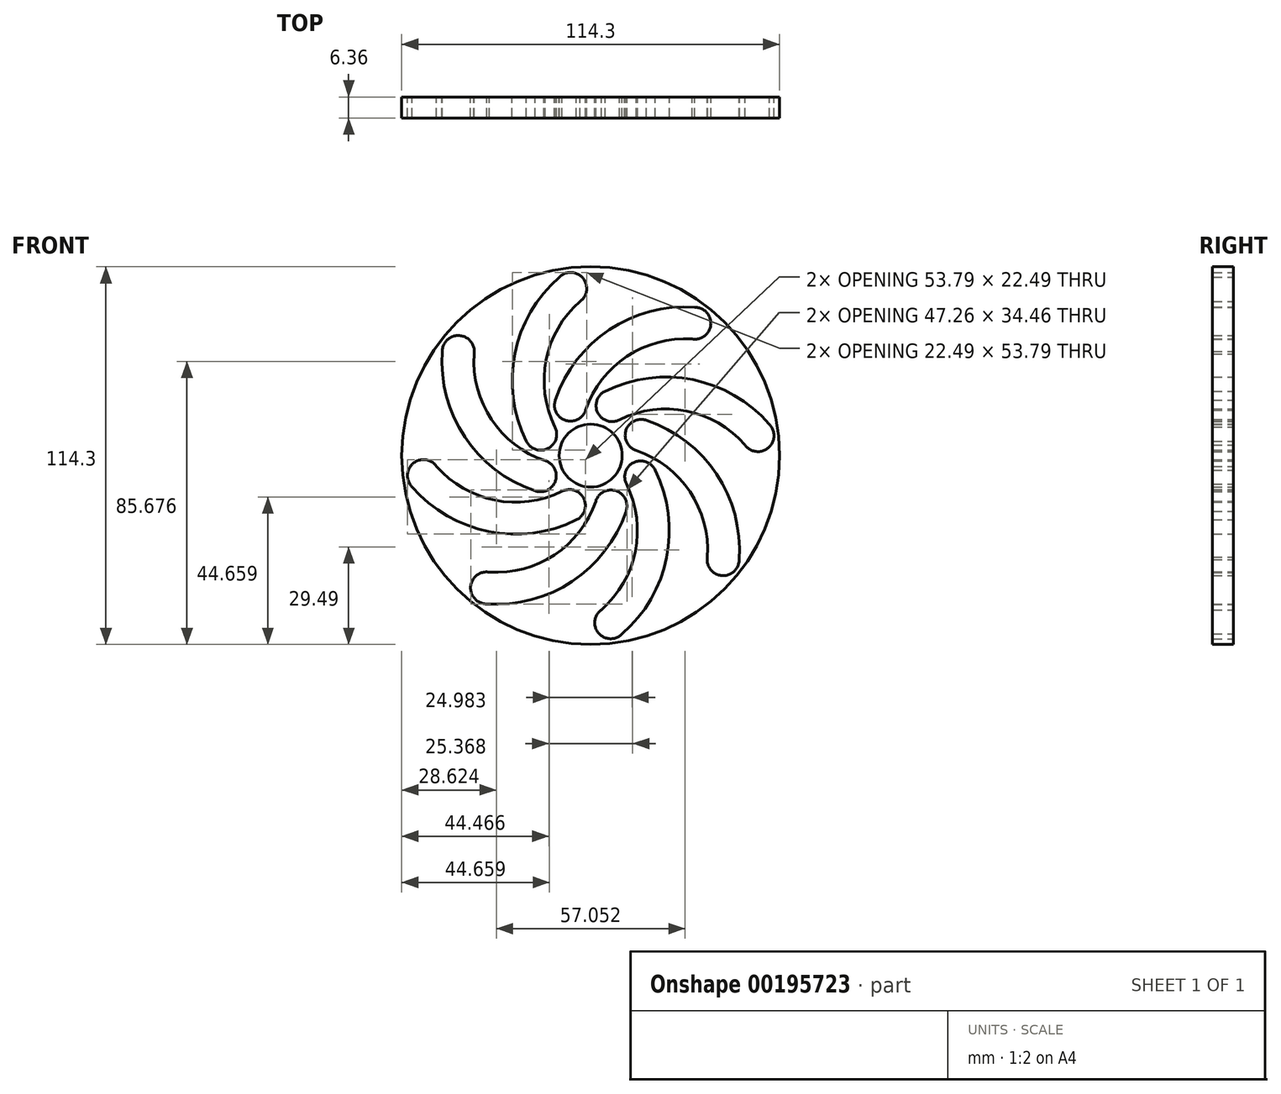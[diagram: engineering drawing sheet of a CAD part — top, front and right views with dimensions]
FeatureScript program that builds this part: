
annotation { "Feature Type Name" : "Feature", "Feature Type Description" : "" }
export const myFeature = defineFeature(function(context is Context, id is Id, definition is map)
    precondition{}
    {
        {
            var Q0;
            Q0=qCreatedBy(makeId("Front.planeOp"),FACE);
            var sketch = newSketch(context, id + "F0", { "sketchPlane" : qUnion([Q0])});
            skCircle(sketch, "E0", {"center": v(0, 0) * mm, "radius": 57.15 * mm});
            skCircle(sketch, "E1", {"center": v(0, 0) * mm, "radius": 9.53 * mm});
            skCircle(sketch, "E2", {"center": v(0, 0) * mm, "radius": 69.85 * mm});
            skArc(sketch, "E3", {"start": v(-35.2, 31.49) * mm, "mid": v(-30.19, 11.2) * mm, "end": v(-13.64, -1.58) * mm});
            skArc(sketch, "E4", {"start": v(-16.85, -10.68) * mm, "mid": v(-10.67, -7.67) * mm, "end": v(-13.78, -1.53) * mm});
            skArc(sketch, "E5", {"start": v(-35.27, 30.71) * mm, "mid": v(-39.66, 36.32) * mm, "end": v(-44.9, 31.49) * mm});
            skArc(sketch, "E6.trimOffspring", {"start": v(-44.83, 32.27) * mm, "mid": v(-38.24, 5.88) * mm, "end": v(-16.7, -10.73) * mm});
            skArc(sketch, "E7.1.0", {"start": v(-47.16, -2.63) * mm, "mid": v(-29.26, -13.43) * mm, "end": v(-8.53, -10.76) * mm});
            skArc(sketch, "E7.1.1", {"start": v(-46.66, -3.22) * mm, "mid": v(-53.72, -2.36) * mm, "end": v(-54, -9.48) * mm});
            skArc(sketch, "E7.1.2", {"start": v(-54.51, -8.88) * mm, "mid": v(-31.2, -22.88) * mm, "end": v(-4.23, -19.4) * mm});
            skArc(sketch, "E7.1.3", {"start": v(-4.36, -19.47) * mm, "mid": v(-2.12, -12.96) * mm, "end": v(-8.66, -10.82) * mm});
            skArc(sketch, "E7.2.0", {"start": v(-31.49, -35.2) * mm, "mid": v(-11.2, -30.19) * mm, "end": v(1.58, -13.64) * mm});
            skArc(sketch, "E7.2.1", {"start": v(-30.71, -35.27) * mm, "mid": v(-36.32, -39.66) * mm, "end": v(-31.49, -44.9) * mm});
            skArc(sketch, "E7.2.2", {"start": v(-32.27, -44.83) * mm, "mid": v(-5.88, -38.24) * mm, "end": v(10.73, -16.7) * mm});
            skArc(sketch, "E7.2.3", {"start": v(10.68, -16.85) * mm, "mid": v(7.67, -10.67) * mm, "end": v(1.53, -13.78) * mm});
            skArc(sketch, "E7.3.0", {"start": v(2.63, -47.16) * mm, "mid": v(13.43, -29.26) * mm, "end": v(10.76, -8.53) * mm});
            skArc(sketch, "E7.3.1", {"start": v(3.22, -46.66) * mm, "mid": v(2.36, -53.72) * mm, "end": v(9.48, -54) * mm});
            skArc(sketch, "E7.3.2", {"start": v(8.88, -54.51) * mm, "mid": v(22.88, -31.2) * mm, "end": v(19.4, -4.23) * mm});
            skArc(sketch, "E7.3.3", {"start": v(19.47, -4.36) * mm, "mid": v(12.96, -2.12) * mm, "end": v(10.82, -8.66) * mm});
            skArc(sketch, "E7.4.0", {"start": v(35.2, -31.49) * mm, "mid": v(30.19, -11.2) * mm, "end": v(13.64, 1.58) * mm});
            skArc(sketch, "E7.4.1", {"start": v(35.27, -30.71) * mm, "mid": v(39.66, -36.32) * mm, "end": v(44.9, -31.49) * mm});
            skArc(sketch, "E7.4.2", {"start": v(44.83, -32.27) * mm, "mid": v(38.24, -5.88) * mm, "end": v(16.7, 10.73) * mm});
            skArc(sketch, "E7.4.3", {"start": v(16.85, 10.68) * mm, "mid": v(10.67, 7.67) * mm, "end": v(13.78, 1.53) * mm});
            skArc(sketch, "E7.5.0", {"start": v(47.16, 2.63) * mm, "mid": v(29.26, 13.43) * mm, "end": v(8.53, 10.76) * mm});
            skArc(sketch, "E7.5.1", {"start": v(46.66, 3.22) * mm, "mid": v(53.72, 2.36) * mm, "end": v(54, 9.48) * mm});
            skArc(sketch, "E7.5.2", {"start": v(54.51, 8.88) * mm, "mid": v(31.2, 22.88) * mm, "end": v(4.23, 19.4) * mm});
            skArc(sketch, "E7.5.3", {"start": v(4.36, 19.47) * mm, "mid": v(2.12, 12.96) * mm, "end": v(8.66, 10.82) * mm});
            skArc(sketch, "E7.6.0", {"start": v(31.49, 35.2) * mm, "mid": v(11.2, 30.19) * mm, "end": v(-1.58, 13.64) * mm});
            skArc(sketch, "E7.6.1", {"start": v(30.71, 35.27) * mm, "mid": v(36.32, 39.66) * mm, "end": v(31.49, 44.9) * mm});
            skArc(sketch, "E7.6.2", {"start": v(32.27, 44.83) * mm, "mid": v(5.88, 38.24) * mm, "end": v(-10.73, 16.7) * mm});
            skArc(sketch, "E7.6.3", {"start": v(-10.68, 16.85) * mm, "mid": v(-7.67, 10.67) * mm, "end": v(-1.53, 13.78) * mm});
            skArc(sketch, "E7.7.0", {"start": v(-2.63, 47.16) * mm, "mid": v(-13.43, 29.26) * mm, "end": v(-10.76, 8.53) * mm});
            skArc(sketch, "E7.7.1", {"start": v(-3.22, 46.66) * mm, "mid": v(-2.36, 53.72) * mm, "end": v(-9.48, 54) * mm});
            skArc(sketch, "E7.7.2", {"start": v(-8.88, 54.51) * mm, "mid": v(-22.88, 31.2) * mm, "end": v(-19.4, 4.23) * mm});
            skArc(sketch, "E7.7.3", {"start": v(-19.47, 4.36) * mm, "mid": v(-12.96, 2.12) * mm, "end": v(-10.82, 8.66) * mm});
            skSolve(sketch);
        }
        {
            var Q0;
            Q0=makeQuery(id+"F0.imprint","IMPRINT",FACE,{"disambiguationData":[TD([[makeQuery(id+"F0.imprint","IMPRINT",EDGE,{"derivedFrom":sQuery(id+"F0.wireOp",EDGE,"E0")}),1.0]])]});
            extrude(context, id + "F1", {"entities" : qUnion([Q0]), "endBound" : BoundingType.SYMMETRIC, "depth" : 6.35 * mm});
        }
    });
